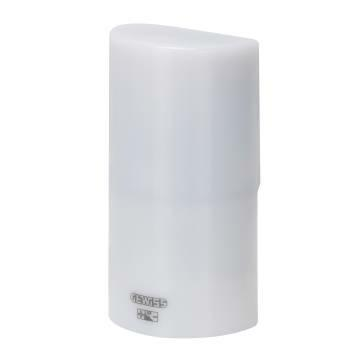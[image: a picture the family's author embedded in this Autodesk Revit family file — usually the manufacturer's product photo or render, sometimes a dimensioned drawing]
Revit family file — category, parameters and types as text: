
# Revit family: Domotics-DomesticRanges-GEWISS-27COMBI_SYSTEM-IP65_PHOTOCELL
name_source: partatom
category: Modelli generici
revit_build: Autodesk Revit 2016 (Build: 20161004_0715(x64)
units: mm (PartAtom-declared; Revit-internal decimal feet)

## family parameters
Condiviso = No
Host = Superficie
Punto di calcolo locali = No
Può ospitare armatura = No
Quota connettore circolare = Usa diametro
Taglio con vuoti quando caricato = No
Tipo di parte = Normale

## types (1)
- GW27432 - Photocell lighting control 2-200lux IP65
    Altezza = 106 mm  [stored 0.347769 ft]
    Catalogue = DOMOTICS
    Catalogue Range = 27COMBI
    Descrizione = PHOTOCELL LIGHTING CONTROL 2-200LUX IP65
    EAN code = 8011564827554
    Electrocod = 0143
    Glow Wire Test = 650°C
    IDF = ed953061-fc2c-4c9a-93d9-9e4612de92e8
    IDT = 09f7fde4-0fd3-4868-bfba-d57139335556
    IP degree = IP65
    Immagine tipo = GW27432.jpg
    Installation temperature = -25 +60 °C
    Insulation class = II
    Larghezza = 55 mm
    Modello = GW27432
    Outer dim. LxHxD (mm) = 55x106x45
    Produttore = GEWISS S.p.A.
    Profondità = 45 mm  [stored 0.147638 ft]
    Prospetto di default = 1219 mm
    Standard = EN 60669-2-1
    Technical sheet = https://www.gewiss.com
    Thermo-pressure with ball = 70
    Treshold adjustment = 0 - 200 lux
    URL = https://www.gewiss.com
    Version file RFA = 18.0

note: source unit labels omitted for Thermo-pressure with ball — the stored unit's dimension contradicts the parameter name (converter mislabeling)

note: [stored X ft] marks values corroborated as IEEE doubles in the binary element streams (Revit-internal decimal feet)

## geometry (parser evidence)
native form markers: Sweep x2
no freeform markers — native parametric forms only
